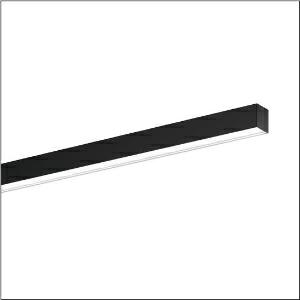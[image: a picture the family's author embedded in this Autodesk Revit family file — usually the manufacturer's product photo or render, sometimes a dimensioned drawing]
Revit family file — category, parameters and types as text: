
# Revit family: silica_r__21_51mx23tat4b_8a74
name_source: partatom
category: Lighting Fixtures
units: mm (PartAtom-declared; Revit-internal decimal feet)

## family parameters
Cut with Voids When Loaded = No
Host = Face
Light Source = No
Part Type = Normal
Room Calculation Point = No
Round Connector Dimension = Use Diameter
Shared = No

## types (1)
- --- (1 x LED, 3230 lm, 32.4 W, 6500K)
    Apparent Load = 32 VA
    CIE Flux Codes = 78 96 99 100 100
    Color Rendering = 80
    Color Temperature = 6500K
    Default Elevation = 1800 mm
    Description = Silica® 21, office luminaire, primary optical cover: prismatic diffuser, of PMMA, CAT 2 (L<= 3000cd/m²), light emission: direct distribution, primary light characteristic: symmetric, installation type: surface-mounted, LED, rated luminous flux: 3.230lm, luminous efficacy: 95lm/W, light colour: 8tw, colour temperature: 2700..6500K, control gear: ECG DALI, with terminal, 3+2-pole, max. 2.5mm², mains connection: 220..240V, AC, 50/60Hz, rated input power: 34W, luminaire housing, of aluminium, jet black (RAL 9005), length: 1.204mm, width: 53mm, height: 53mm, protection rating (complete): IP20, insulation class (complete): insulation class I (protective earthing), certification: CE, permissible operating ambient temperature: 0..+35°C, standard: EN 50419, packaging unit: 1 piece
    Height = 0 mm  [stored 0 ft]
    Lamp = 1 x LED
    Lamp Light Flux = 3230 lm
    Lamp Power = 32.4 W
    Lamp count = 1
    Length = 1204 mm
    Luminous efficacy = 100 lm/W
    Manufacturer = Siteco
    ModVariant = No
    Model = 51MX23TAT4B
    Mounting Place = Ceiling
    Mounting Type = Recessed
    Number of Poles = 1
    OnlyDefault = Yes
    Power Factor = 1
    Product Name = Silica® 21
    Product group = office luminaire | ceiling recessed
    ProductGroupID = 400
    Protection Class = Protection class I
    Protection Degree = IP 20
    RLX_Detail_Level = 1
    RLX_Emergency_Light_Flux = 0 lm
    RLX_Emergency_Type = 0
    RLX_Emergency_Type_DB = No
    RlxData = <blob elided: 20505 chars, md5=70aa1efb>
    Socket = socket
    Standby Power = 0 W
    System Light Flux = 3230 lm
    System Power = 32 W
    Type Comments = individual setting
    Type Image = l_1335925.jpg
    URL = http://relux.com
    VarID = @adj_109621
    Voltage = 0 V
    Weight = 0.00 kg
    Width = 53 mm

note: [stored X ft] marks values corroborated as IEEE doubles in the binary element streams (Revit-internal decimal feet)

## geometry (parser evidence)
native form markers: Blend x4, Sweep x9
no freeform markers — native parametric forms only
